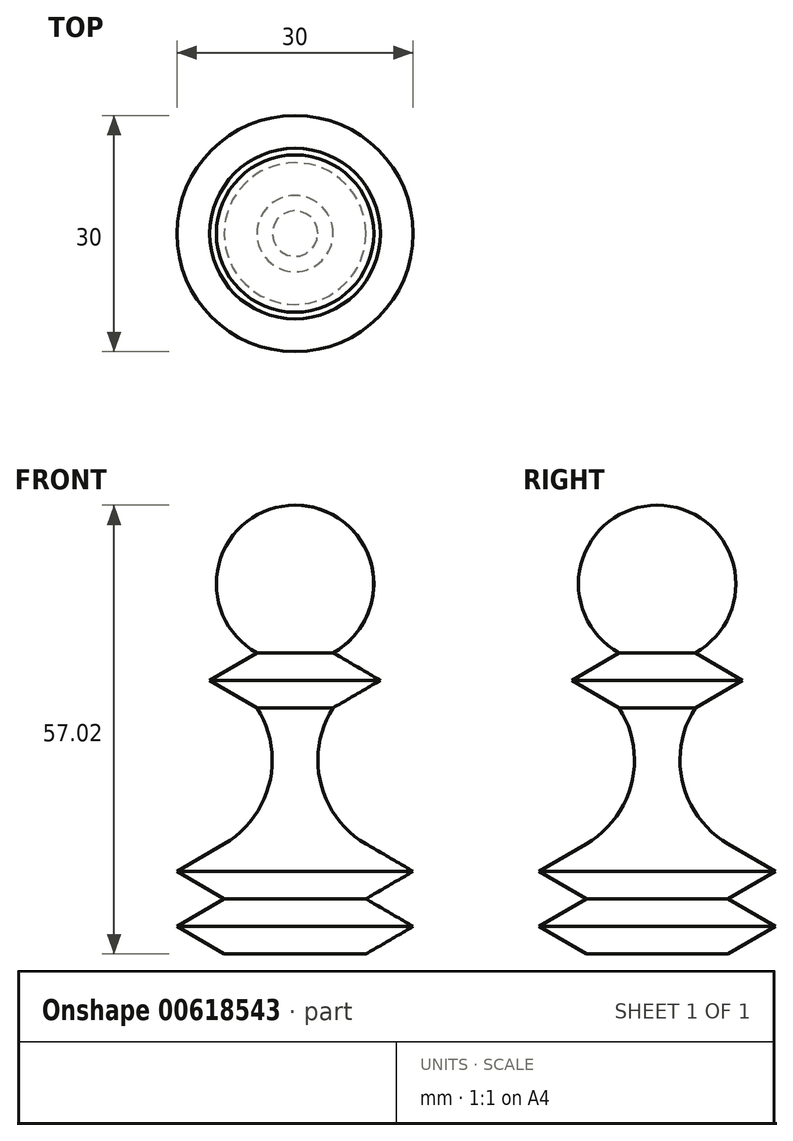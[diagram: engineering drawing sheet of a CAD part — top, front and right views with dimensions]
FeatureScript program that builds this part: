
annotation { "Feature Type Name" : "Feature", "Feature Type Description" : "" }
export const myFeature = defineFeature(function(context is Context, id is Id, definition is map)
    precondition{}
    {
        {
            var Q0;
            Q0=qCreatedBy(makeId("Front.planeOp"),FACE);
            var sketch = newSketch(context, id + "F0", { "sketchPlane" : qUnion([Q0])});
            skLineSegment(sketch, "E0", {"start": v(0, 0) * mm, "end": v(9, 0) * mm});
            skLineSegment(sketch, "E1", {"start": v(9, 0) * mm, "end": v(15, 3.5) * mm});
            skLineSegment(sketch, "E2", {"start": v(15, 3.5) * mm, "end": v(9, 7) * mm});
            skLineSegment(sketch, "E3", {"start": v(9, 7) * mm, "end": v(15, 10.5) * mm});
            skLineSegment(sketch, "E4", {"start": v(15, 10.5) * mm, "end": v(9, 14) * mm});
            skArc(sketch, "E5", {"start": v(4.84, 31.27) * mm, "mid": v(3.24, 21.75) * mm, "end": v(9, 14) * mm});
            skLineSegment(sketch, "E6", {"start": v(4.84, 31.27) * mm, "end": v(10.84, 34.77) * mm});
            skLineSegment(sketch, "E7", {"start": v(10.84, 34.77) * mm, "end": v(4.84, 38.27) * mm});
            skArc(sketch, "E8", {"start": v(4.84, 38.27) * mm, "mid": v(9.68, 49.52) * mm, "end": v(0, 57.02) * mm});
            skLineSegment(sketch, "E9", {"start": v(0, 57.02) * mm, "end": v(0, 0) * mm});
            skSolve(sketch);
        }
        {
            var Q0;
            Q0=makeQuery(id+"F0.imprint","IMPRINT",FACE,{"disambiguationData":[TD([[makeQuery(id+"F0.imprint","IMPRINT",EDGE,{"derivedFrom":sQuery(id+"F0.wireOp",EDGE,"E0")}),1.0]])]});
            var Q1;
            Q1=sQuery(id+"F0.wireOp",EDGE,"E9");
            revolve(context, id + "F1", {"entities" : qUnion([Q0]), "axis" : qUnion([Q1]), "revolveType" : RevolveType.FULL});
        }
    });
